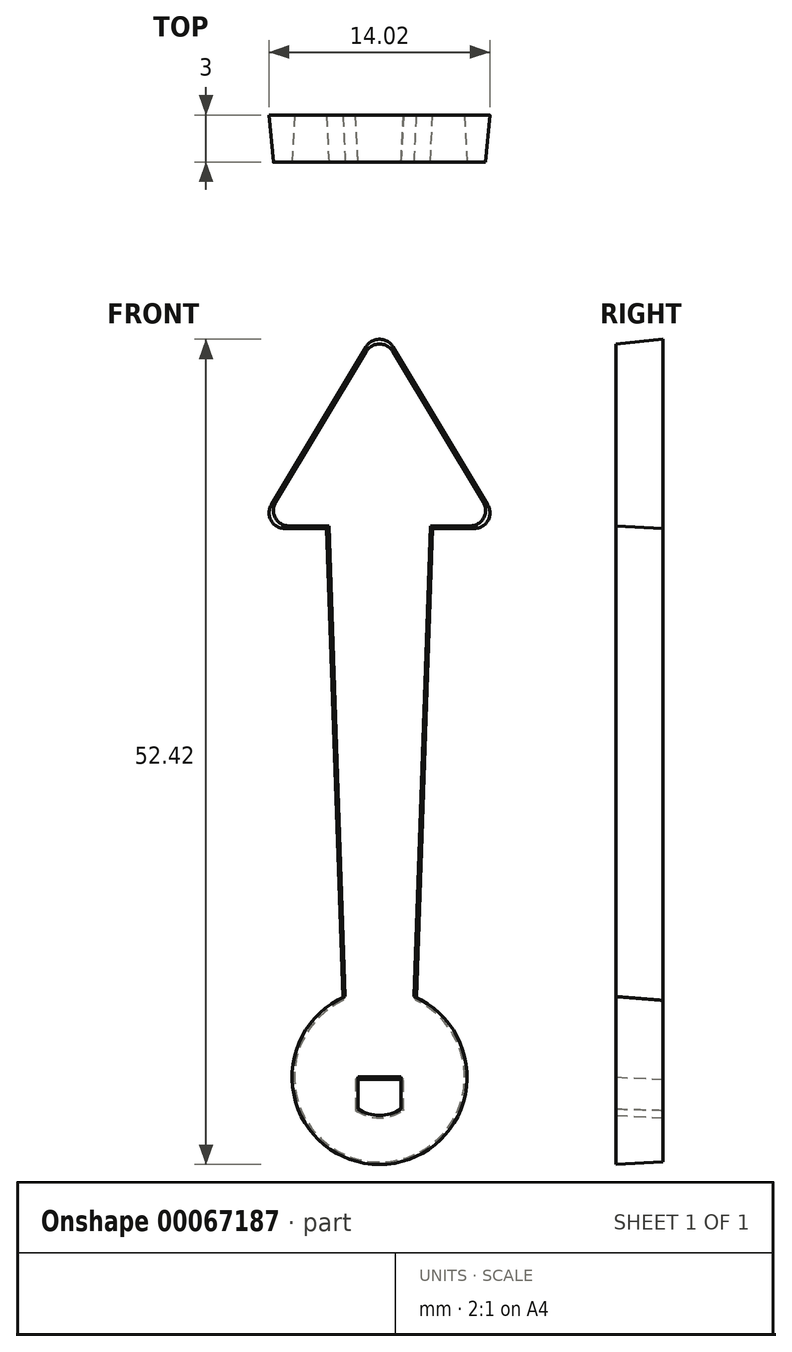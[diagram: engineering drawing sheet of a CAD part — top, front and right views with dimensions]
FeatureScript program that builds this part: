
annotation { "Feature Type Name" : "Feature", "Feature Type Description" : "" }
export const myFeature = defineFeature(function(context is Context, id is Id, definition is map)
    precondition{}
    {
        {
            var Q0;
            Q0=qCreatedBy(makeId("Front.planeOp"),FACE);
            var sketch = newSketch(context, id + "F0", { "sketchPlane" : qUnion([Q0])});
            skCircle(sketch, "E0", {"center": v(0, 0) * mm, "radius": 5.4 * mm});
            skCircle(sketch, "E1", {"center": v(0, 0) * mm, "radius": 2.6 * mm});
            skLineSegment(sketch, "E2", {"start": v(-1.52, -2.1) * mm, "end": v(-1.52, 2.1) * mm});
            skLineSegment(sketch, "E3", {"start": v(1.52, -2.1) * mm, "end": v(1.52, 2.1) * mm});
            skSolve(sketch);
        }
        {
            var Q0;
            Q0 = qSketchRegion(id + "F0", true);
            var Q1;
            {var subQ0=sQuery(id+"F0.wireOp",EDGE,"E3");Q1=makeQuery(id+"F0.imprint","IMPRINT",FACE,{"disambiguationData":[TD([[makeQuery(id+"F0.imprint","IMPRINT",EDGE,{"derivedFrom":subQ0}),-1.0]])]});}
            var Q2;
            {var subQ0=sQuery(id+"F0.wireOp",EDGE,"E2");Q2=makeQuery(id+"F0.imprint","IMPRINT",FACE,{"disambiguationData":[TD([[makeQuery(id+"F0.imprint","IMPRINT",EDGE,{"derivedFrom":subQ0}),1.0]])]});}
            extrude(context, id + "F1", {"entities" : qUnion([Q0, Q1, Q2]), "depth" : 3 * mm, "hasDraft" : true, "draftAngle" : 3 * degree});
        }
        {
            var Q0;
            Q0=makeQuery(id+"F1.opExtrude","CAP_FACE",FACE,{"disambiguationData":[OSD([sQuery(id+"F0.wireOp",EDGE,"E0"),sQuery(id+"F0.wireOp",EDGE,"E1"),sQuery(id+"F0.wireOp",EDGE,"E2"),sQuery(id+"F0.wireOp",EDGE,"E3")])],"isStart":false});
            var sketch = newSketch(context, id + "F2", { "sketchPlane" : qUnion([Q0])});
            skLineSegment(sketch, "E4", {"start": v(0, 0) * mm, "end": v(0, 35) * mm, "construction": true});
            skLineSegment(sketch, "E5", {"start": v(0, 35) * mm, "end": v(3.22, 35) * mm});
            skLineSegment(sketch, "E6", {"start": v(0, 0) * mm, "end": v(2, 0) * mm});
            skPoint(sketch, "E6.endSnap0", {"position": v(1.37, 0) * mm});
            skLineSegment(sketch, "E7", {"start": v(2, 0) * mm, "end": v(3.22, 35) * mm});
            skLineSegment(sketch, "E8.MirrorCS", {"start": v(0, 35) * mm, "end": v(-3.22, 35) * mm});
            skLineSegment(sketch, "E9.MirrorCS", {"start": v(-2, 0) * mm, "end": v(-3.22, 35) * mm});
            skLineSegment(sketch, "E10.MirrorCS", {"start": v(0, 0) * mm, "end": v(-2, 0) * mm});
            skSolve(sketch);
        }
        {
            var Q0;
            Q0 = qSketchRegion(id + "F2", true);
            extrude(context, id + "F3", {"entities" : qUnion([Q0]), "operationType" : NewBodyOperationType.ADD, "oppositeDirection" : true, "depth" : 3 * mm, "hasDraft" : true, "draftAngle" : 3 * degree});
        }
        {
            var Q0;
            Q0=makeQuery(id+"F3.boolean.opBoolean","MERGE",FACE,{"derivedFrom":[makeQuery(id+"F1.opExtrude","CAP_FACE",FACE,{"disambiguationData":[OSD([sQuery(id+"F0.wireOp",EDGE,"E0"),sQuery(id+"F0.wireOp",EDGE,"E1"),sQuery(id+"F0.wireOp",EDGE,"E2"),sQuery(id+"F0.wireOp",EDGE,"E3")])],"isStart":false}),makeQuery(id+"F3.opExtrude","CAP_FACE",FACE,{"disambiguationData":[OSD([sQuery(id+"F2.wireOp",EDGE,"E5"),sQuery(id+"F2.wireOp",EDGE,"E6"),sQuery(id+"F2.wireOp",EDGE,"E7"),sQuery(id+"F2.wireOp",EDGE,"E8.MirrorCS"),sQuery(id+"F2.wireOp",EDGE,"E9.MirrorCS"),sQuery(id+"F2.wireOp",EDGE,"E10.MirrorCS")])],"isStart":true})]});
            var sketch = newSketch(context, id + "F4", { "sketchPlane" : qUnion([Q0])});
            skLineSegment(sketch, "E11", {"start": v(0, 35) * mm, "end": v(0, 47.5) * mm, "construction": true});
            skPoint(sketch, "E11.endSnap0", {"position": v(0, 35) * mm});
            skLineSegment(sketch, "E12", {"start": v(-7.5, 35) * mm, "end": v(0, 47.5) * mm});
            skLineSegment(sketch, "E13", {"start": v(0, 47.5) * mm, "end": v(7.5, 35) * mm});
            skLineSegment(sketch, "E14", {"start": v(-7.5, 35) * mm, "end": v(7.5, 35) * mm});
            skSolve(sketch);
        }
        {
            var Q0;
            {var subQ4=sQuery(id+"F4.wireOp",EDGE,"E12");Q0=makeQuery(id+"F4.imprint","IMPRINT",FACE,{"disambiguationData":[TD([[makeQuery(id+"F4.imprint","IMPRINT",EDGE,{"derivedFrom":subQ4}),-1.0]])]});}
            extrude(context, id + "F5", {"entities" : qUnion([Q0]), "operationType" : NewBodyOperationType.ADD, "oppositeDirection" : true, "depth" : 3 * mm, "hasDraft" : true, "draftAngle" : 3 * degree});
        }
        {
            var Q0;
            Q0=makeQuery(id+"F5.opExtrude","SWEPT_EDGE",EDGE,{"disambiguationData":[OSD([sQuery(id+"F4.wireOp",EDGE,"E12"),sQuery(id+"F4.wireOp",EDGE,"E13")])]});
            var Q1;
            Q1=makeQuery(id+"F5.opExtrude","SWEPT_EDGE",EDGE,{"disambiguationData":[OSD([sQuery(id+"F4.wireOp",EDGE,"E12"),sQuery(id+"F4.wireOp",EDGE,"E14")])]});
            var Q2;
            Q2=makeQuery(id+"F5.opExtrude","SWEPT_EDGE",EDGE,{"disambiguationData":[OSD([sQuery(id+"F4.wireOp",EDGE,"E13"),sQuery(id+"F4.wireOp",EDGE,"E14")])]});
            fillet(context, id + "F6", {"entities" : qUnion([Q0, Q1, Q2]), "radius" : 1 * mm, "tangentPropagation" : true, "allowEdgeOverflow" : false});
        }
    });
